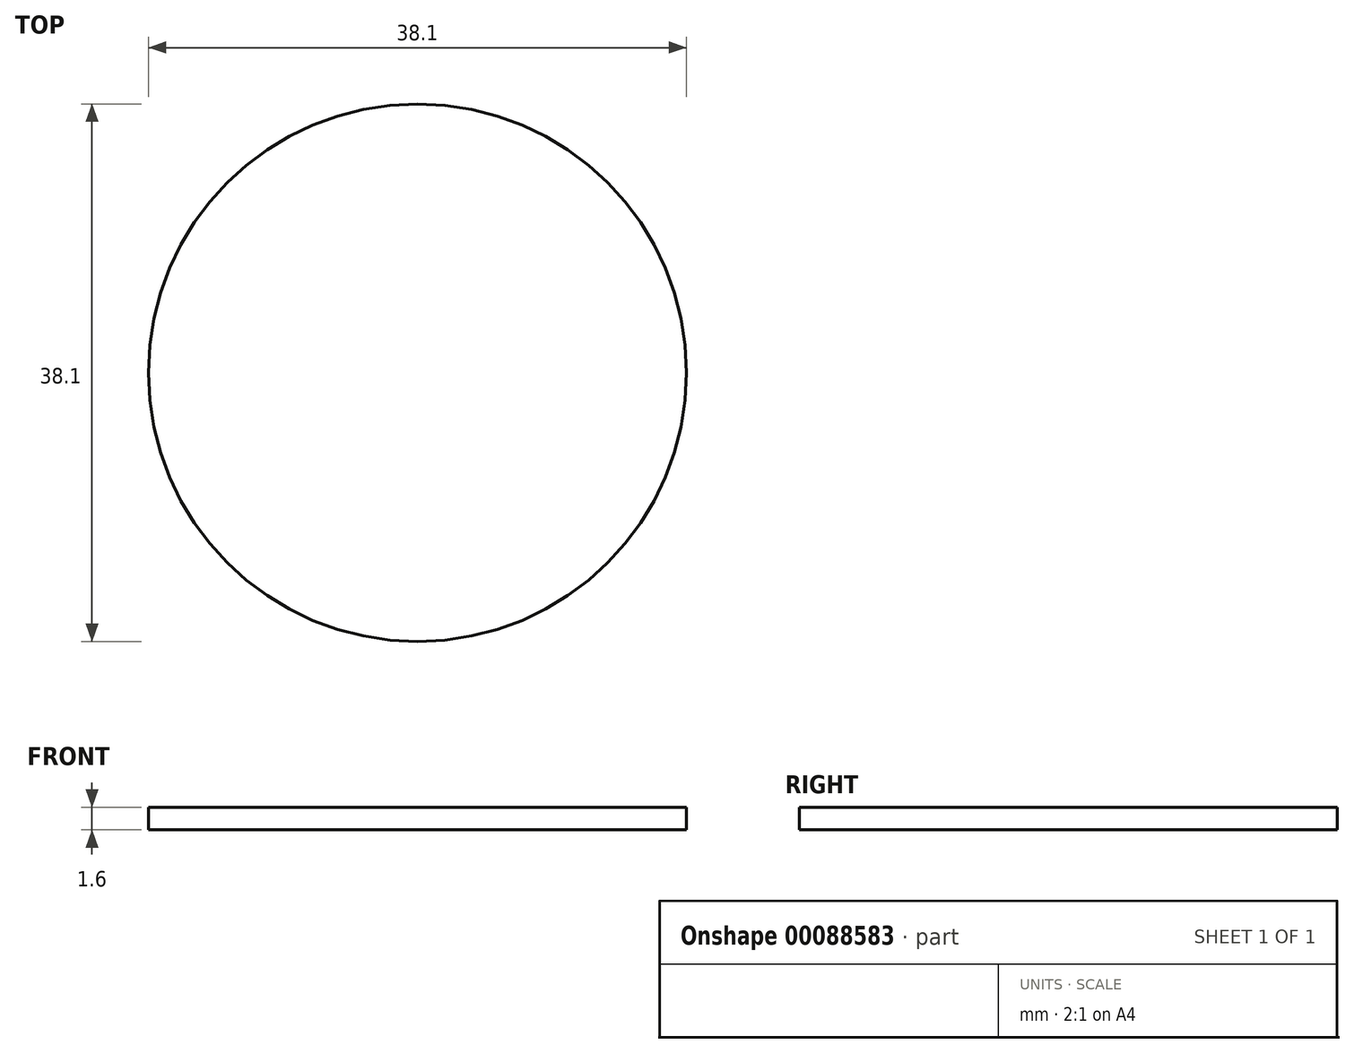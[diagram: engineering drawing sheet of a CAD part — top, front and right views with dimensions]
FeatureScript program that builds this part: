
annotation { "Feature Type Name" : "Feature", "Feature Type Description" : "" }
export const myFeature = defineFeature(function(context is Context, id is Id, definition is map)
    precondition{}
    {
        {
            var Q0;
            Q0=qCreatedBy(makeId("Top.planeOp"),FACE);
            var sketch = newSketch(context, id + "F0", { "sketchPlane" : qUnion([Q0])});
            skCircle(sketch, "E0", {"center": v(0, 0) * mm, "radius": 19.05 * mm});
            skSolve(sketch);
        }
        {
            var Q0;
            Q0=qSketchRegion(id+"F0",true);
            extrude(context, id + "F1", {"entities" : qUnion([Q0]), "depth" : 1.6 * mm});
        }
    });
